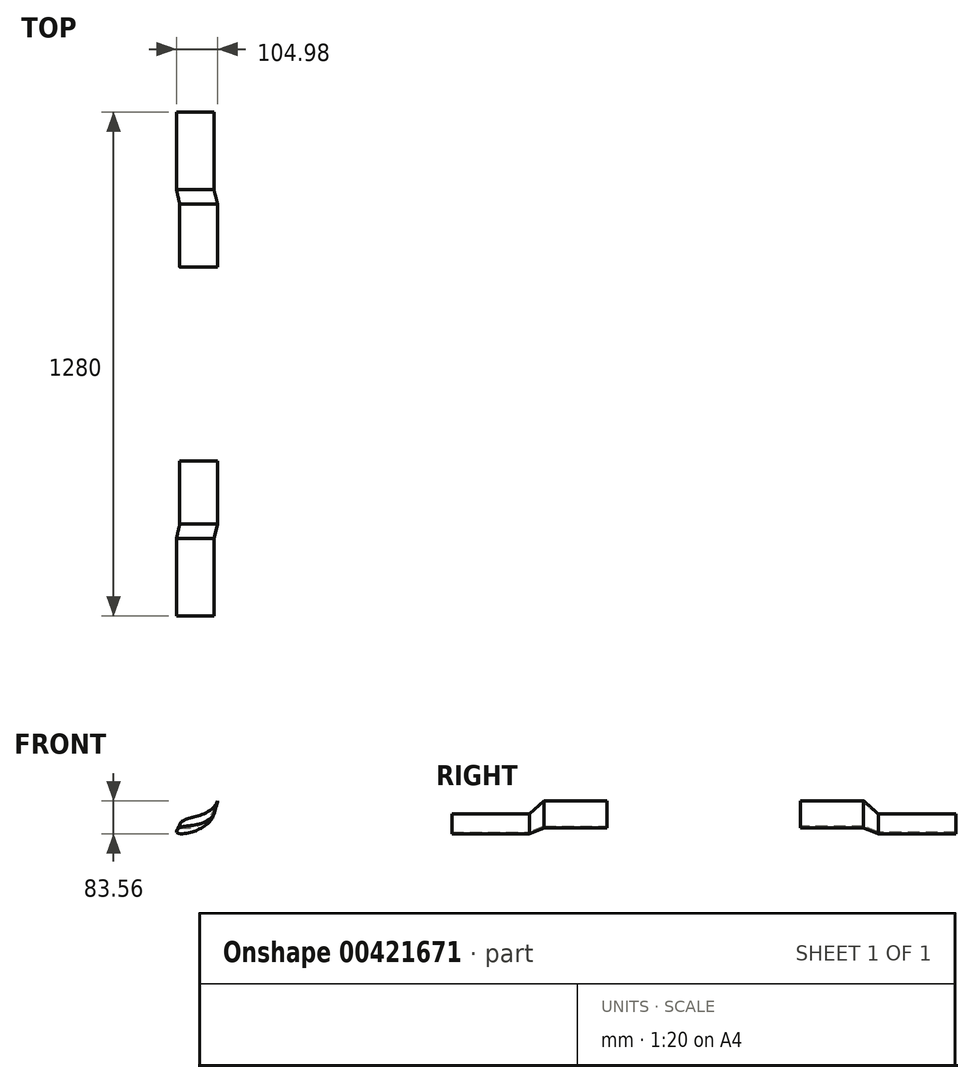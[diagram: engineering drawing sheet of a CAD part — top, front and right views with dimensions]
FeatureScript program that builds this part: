
annotation { "Feature Type Name" : "Feature", "Feature Type Description" : "" }
export const myFeature = defineFeature(function(context is Context, id is Id, definition is map)
    precondition{}
    {
        {
            var Q0;
            Q0=qCreatedBy(makeId("Front.planeOp"),FACE);
            cPlane(context, id + "F0", {"entities" : qUnion([Q0]), "cplaneType" : CPlaneType.OFFSET, "offset" : 246 * mm, "width" : 150 * mm, "height" : 150 * mm});
        }
        {
            var Q0;
            Q0=qCreatedBy(id+"F0.planeOp",FACE);
            var sketch = newSketch(context, id + "F1", { "sketchPlane" : qUnion([Q0])});
            skFitSpline(sketch, "E0", {"points": [v(-996.34, 250.12) * mm, v(-986.5, 265.12) * mm, v(-948.3, 277.08) * mm, v(-900.02, 314.54) * mm], "startDerivative": vector(-16.4, 98.46) * mm, "endDerivative": vector(72.1, 160.24) * mm});
            skFitSpline(sketch, "E1", {"points": [v(-996.34, 250.12) * mm, v(-972.9, 246.14) * mm, v(-927.66, 266.3) * mm, v(-900.02, 314.54) * mm], "startDerivative": vector(37.93, -56.6) * mm, "endDerivative": vector(29.76, 145.5) * mm});
            skSolve(sketch);
        }
        {
            var Q0;
            Q0=qCreatedBy(id+"F0.planeOp",FACE);
            cPlane(context, id + "F2", {"entities" : qUnion([Q0]), "cplaneType" : CPlaneType.OFFSET, "offset" : 197 * mm, "width" : 150 * mm, "height" : 150 * mm});
        }
        {
            var Q0;
            Q0=qCreatedBy(id+"F2.planeOp",FACE);
            var sketch = newSketch(context, id + "F3", { "sketchPlane" : qUnion([Q0])});
            skFitSpline(sketch, "E2", {"points": [v(-1004.98, 234.76) * mm, v(-992.02, 248.14) * mm, v(-954.39, 254) * mm, v(-910.03, 281.41) * mm], "startDerivative": vector(-5.08, 76.25) * mm, "endDerivative": vector(48.08, 106.12) * mm});
            skFitSpline(sketch, "E3", {"points": [v(-1004.98, 234.76) * mm, v(-974.65, 233.33) * mm, v(-940.8, 246.4) * mm, v(-910.03, 281.41) * mm], "startDerivative": vector(37.93, -56.6) * mm, "endDerivative": vector(24.83, 130.35) * mm});
            skSolve(sketch);
        }
        {
            var Q0;
            Q0 = qSketchRegion(id + "F3", true);
            extrude(context, id + "F4", {"entities" : qUnion([Q0]), "depth" : 197 * mm});
        }
        {
            var Q0;
            Q0 = qSketchRegion(id + "F1", true);
            extrude(context, id + "F5", {"entities" : qUnion([Q0]), "depth" : 160 * mm});
        }
        {
            var Q0;
            Q0=makeQuery(id+"F5.opExtrude","CAP_FACE",FACE,{"disambiguationData":[OSD([sQuery(id+"F1.wireOp",EDGE,"E0"),sQuery(id+"F1.wireOp",EDGE,"E1")])],"isStart":false});
            var Q1;
            Q1=makeQuery(id+"F4.opExtrude","CAP_FACE",FACE,{"disambiguationData":[OSD([sQuery(id+"F3.wireOp",EDGE,"E2"),sQuery(id+"F3.wireOp",EDGE,"E3")])],"isStart":true});
            loft(context, id + "F6", {"sheetProfilesArray" : [{ "sheetProfileEntities" : qUnion([Q0]) }, { "sheetProfileEntities" : qUnion([Q1]) }]});
        }
        {
            var Q0;
            Q0=makeQuery(id+"F5.opExtrude","SWEPT_BODY",BODY,{"disambiguationData":[OSD([sQuery(id+"F1.wireOp",EDGE,"E0"),sQuery(id+"F1.wireOp",EDGE,"E1")])]});
            var Q1;
            Q1=makeQuery(id+"F6.opLoft","SWEPT_BODY",BODY,{"disambiguationData":[OSD([sQuery(id+"F1.wireOp",EDGE,"E0"),sQuery(id+"F1.wireOp",EDGE,"E1"),sQuery(id+"F3.wireOp",EDGE,"E2"),sQuery(id+"F3.wireOp",EDGE,"E3")])]});
            var Q2;
            Q2=makeQuery(id+"F4.opExtrude","SWEPT_BODY",BODY,{"disambiguationData":[OSD([sQuery(id+"F3.wireOp",EDGE,"E2"),sQuery(id+"F3.wireOp",EDGE,"E3")])]});
            var Q3;
            Q3=qCreatedBy(makeId("Front.planeOp"),FACE);
            mirror(context, id + "F7", {"entities" : qUnion([Q0, Q1, Q2]), "mirrorPlane" : qUnion([Q3])});
        }
    });
